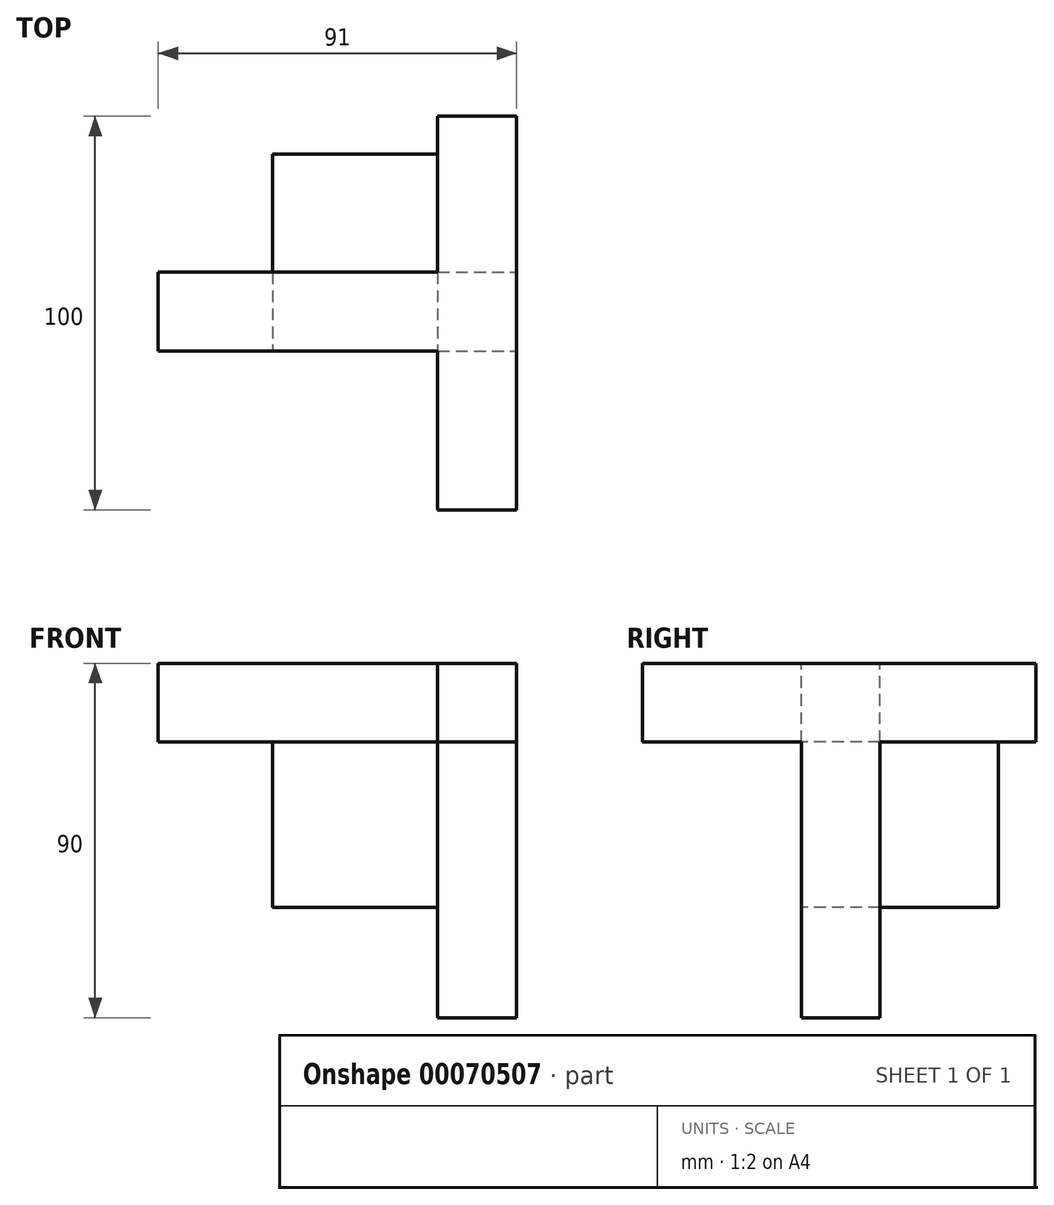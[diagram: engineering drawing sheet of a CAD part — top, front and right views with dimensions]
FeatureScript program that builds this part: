
annotation { "Feature Type Name" : "Feature", "Feature Type Description" : "" }
export const myFeature = defineFeature(function(context is Context, id is Id, definition is map)
    precondition{}
    {
        {
            var Q0;
            Q0=qCreatedBy(makeId("Front.planeOp"),FACE);
            var sketch = newSketch(context, id + "F0", { "sketchPlane" : qUnion([Q0])});
            skLineSegment(sketch, "E0.rect.bottom", {"start": v(10, 10) * mm, "end": v(-10, 10) * mm});
            skLineSegment(sketch, "E0.rect.top", {"start": v(10, -10) * mm, "end": v(-10, -10) * mm});
            skLineSegment(sketch, "E0.rect.left", {"start": v(10, 10) * mm, "end": v(10, -10) * mm});
            skLineSegment(sketch, "E0.rect.right", {"start": v(-10, 10) * mm, "end": v(-10, -10) * mm});
            skPoint(sketch, "E0.rect.middle", {"position": v(0, 0) * mm});
            skSolve(sketch);
        }
        {
            var Q0;
            Q0 = qSketchRegion(id + "F0", true);
            extrude(context, id + "F1", {"entities" : qUnion([Q0]), "depth" : 100 * mm});
        }
        {
            var Q0;
            Q0=makeQuery(id+"F1.opExtrude","SWEPT_FACE",FACE,{"disambiguationData":[OSD([sQuery(id+"F0.wireOp",EDGE,"E0.rect.right")])]});
            var sketch = newSketch(context, id + "F2", { "sketchPlane" : qUnion([Q0])});
            skLineSegment(sketch, "E1.bottom", {"start": v(59.61, -10) * mm, "end": v(39.61, -10) * mm});
            skLineSegment(sketch, "E1.top", {"start": v(59.61, 10) * mm, "end": v(39.61, 10) * mm});
            skLineSegment(sketch, "E1.left", {"start": v(59.61, -10) * mm, "end": v(59.61, 10) * mm});
            skLineSegment(sketch, "E1.right", {"start": v(39.61, -10) * mm, "end": v(39.61, 10) * mm});
            skSolve(sketch);
        }
        {
            var Q0;
            Q0 = qSketchRegion(id + "F2", true);
            extrude(context, id + "F3", {"entities" : qUnion([Q0]), "operationType" : NewBodyOperationType.ADD, "depth" : 71 * mm});
        }
        {
            var Q0;
            Q0=makeQuery(id+"F3.boolean.opBoolean","MERGE",FACE,{"derivedFrom":[makeQuery(id+"F1.opExtrude","SWEPT_FACE",FACE,{"disambiguationData":[OSD([sQuery(id+"F0.wireOp",EDGE,"E0.rect.top")])]}),makeQuery(id+"F3.opExtrude","SWEPT_FACE",FACE,{"disambiguationData":[OSD([sQuery(id+"F2.wireOp",EDGE,"E1.bottom")])]})]});
            var sketch = newSketch(context, id + "F4", { "sketchPlane" : qUnion([Q0])});
            skLineSegment(sketch, "E2.bottom", {"start": v(-10, 59.61) * mm, "end": v(10, 59.61) * mm});
            skLineSegment(sketch, "E2.top", {"start": v(-10, 39.61) * mm, "end": v(10, 39.61) * mm});
            skLineSegment(sketch, "E2.left", {"start": v(-10, 59.61) * mm, "end": v(-10, 39.61) * mm});
            skLineSegment(sketch, "E2.right", {"start": v(10, 59.61) * mm, "end": v(10, 39.61) * mm});
            skSolve(sketch);
        }
        {
            var Q0;
            Q0 = qSketchRegion(id + "F4", true);
            extrude(context, id + "F5", {"entities" : qUnion([Q0]), "operationType" : NewBodyOperationType.ADD, "depth" : 70 * mm});
        }
        {
            var Q0;
            Q0=makeQuery(id+"F5.opExtrude","SWEPT_FACE",FACE,{"disambiguationData":[OSD([sQuery(id+"F4.wireOp",EDGE,"E2.bottom")])]});
            var sketch = newSketch(context, id + "F6", { "sketchPlane" : qUnion([Q0])});
            skSolve(sketch);
        }
        {
            var Q0;
            {var subQ0=sQuery(id+"F4.wireOp",EDGE,"E2.bottom");Q0=makeQuery(id+"F6.imprint","IMPRINT",FACE,{"disambiguationData":[TD([[makeQuery(id+"F6.imprint","IMPRINT",EDGE,{"derivedFrom":makeQuery(id+"F5.opExtrude","CAP_EDGE",EDGE,{"disambiguationData":[OSD([subQ0])],"isStart":false})}),1.0]])]});}
            var sketch = newSketch(context, id + "F7", { "sketchPlane" : qUnion([Q0])});
            skPoint(sketch, "E3.0", {"position": v(-10, -10) * mm});
            skLineSegment(sketch, "E4.bottom", {"start": v(-10, -10) * mm, "end": v(-52, -10) * mm});
            skLineSegment(sketch, "E4.top", {"start": v(-10, -52) * mm, "end": v(-52, -52) * mm});
            skLineSegment(sketch, "E4.left", {"start": v(-10, -10) * mm, "end": v(-10, -52) * mm});
            skLineSegment(sketch, "E4.right", {"start": v(-52, -10) * mm, "end": v(-52, -52) * mm});
            skCircle(sketch, "E5", {"center": v(-31, -31) * mm, "radius": 13.1 * mm});
            skPoint(sketch, "E5.centerSnap0", {"position": v(-52, -31) * mm});
            skPoint(sketch, "E5.centerSnap1", {"position": v(-31, -10) * mm});
            skSolve(sketch);
        }
        {
            var Q0;
            Q0 = qSketchRegion(id + "F7", true);
            var Q1;
            Q1=makeQuery(id+"F7.imprint","IMPRINT",FACE,{"disambiguationData":[TD([[makeQuery(id+"F7.imprint","IMPRINT",EDGE,{"derivedFrom":sQuery(id+"F7.wireOp",EDGE,"E5")}),1.0]])]});
            extrude(context, id + "F8", {"entities" : qUnion([Q0, Q1]), "oppositeDirection" : true, "depth" : 50 * mm});
        }
    });
